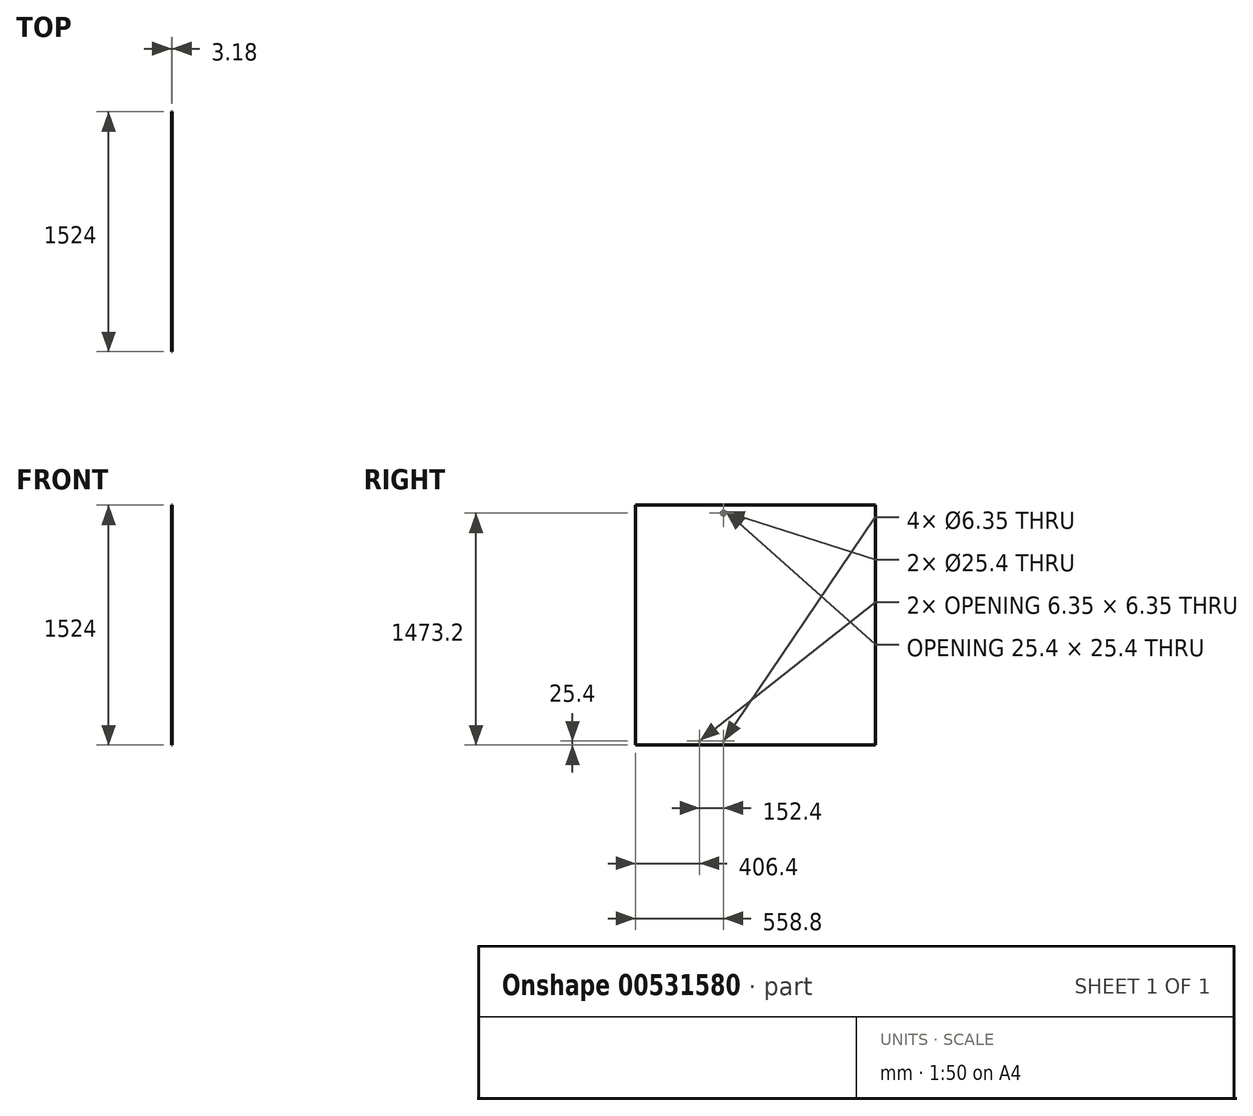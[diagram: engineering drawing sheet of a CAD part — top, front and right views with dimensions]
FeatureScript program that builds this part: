
annotation { "Feature Type Name" : "Feature", "Feature Type Description" : "" }
export const myFeature = defineFeature(function(context is Context, id is Id, definition is map)
    precondition{}
    {
        {
            var Q0;
            Q0=qCreatedBy(makeId("Right.planeOp"),FACE);
            var sketch = newSketch(context, id + "F0", { "sketchPlane" : qUnion([Q0])});
            skLineSegment(sketch, "E0.bottom", {"start": v(0, 0) * mm, "end": v(0, 0) * mm});
            skLineSegment(sketch, "E0.top", {"start": v(0, 0) * mm, "end": v(0, 0) * mm});
            skLineSegment(sketch, "E0.left", {"start": v(0, 0) * mm, "end": v(0, 0) * mm});
            skLineSegment(sketch, "E0.right", {"start": v(0, 0) * mm, "end": v(0, 0) * mm});
            skLineSegment(sketch, "E1.bottom", {"start": v(1524, 1524) * mm, "end": v(0, 1524) * mm});
            skLineSegment(sketch, "E1.top", {"start": v(1524, 0) * mm, "end": v(0, 0) * mm});
            skLineSegment(sketch, "E1.left", {"start": v(1524, 1524) * mm, "end": v(1524, 0) * mm});
            skLineSegment(sketch, "E1.right", {"start": v(0, 1524) * mm, "end": v(0, 0) * mm});
            skPoint(sketch, "E2", {"position": v(406.4, 25.4) * mm});
            skPoint(sketch, "E3", {"position": v(558.8, 25.4) * mm});
            skPoint(sketch, "E4", {"position": v(558.8, 1473.2) * mm});
            skSolve(sketch);
        }
        {
            var Q0;
            Q0=makeQuery(id+"F0.imprint","IMPRINT",FACE,{"disambiguationData":[TD([[makeQuery(id+"F0.imprint","IMPRINT",EDGE,{"derivedFrom":sQuery(id+"F0.wireOp",EDGE,"E1.bottom")}),1.0]])]});
            extrude(context, id + "F1", {"entities" : qUnion([Q0]), "depth" : 3.17 * mm, "offsetDistance" : 25.4 * mm});
        }
        {
            var Q0;
            Q0=sQuery(id+"F0.wireOp",VERTEX,"E2");
            var Q1;
            Q1=makeQuery(id+"F1.opExtrude","SWEPT_BODY",BODY,{"disambiguationData":[OSD([sQuery(id+"F0.wireOp",EDGE,"E1.bottom"),sQuery(id+"F0.wireOp",EDGE,"E1.top"),sQuery(id+"F0.wireOp",EDGE,"E1.left"),sQuery(id+"F0.wireOp",EDGE,"E1.right")])]});
            hole(context, id + "F2", {"style" : HoleStyle.SIMPLE, "endStyle" : HoleEndStyle.THROUGH, "oppositeDirection" : true, "holeDiameter" : 6.35 * mm, "isTappedThrough" : true, "tappedDepth" : 12.7 * mm, "tapClearance" : 3, "locations" : qUnion([Q0]), "scope" : qUnion([Q1])});
        }
        {
            var Q0;
            Q0=sQuery(id+"F0.wireOp",VERTEX,"E3");
            var Q1;
            Q1=makeQuery(id+"F1.opExtrude","SWEPT_BODY",BODY,{"disambiguationData":[OSD([sQuery(id+"F0.wireOp",EDGE,"E1.bottom"),sQuery(id+"F0.wireOp",EDGE,"E1.top"),sQuery(id+"F0.wireOp",EDGE,"E1.left"),sQuery(id+"F0.wireOp",EDGE,"E1.right")])]});
            hole(context, id + "F3", {"style" : HoleStyle.SIMPLE, "endStyle" : HoleEndStyle.THROUGH, "oppositeDirection" : true, "holeDiameter" : 6.35 * mm, "isTappedThrough" : true, "tappedDepth" : 12.7 * mm, "tapClearance" : 3, "locations" : qUnion([Q0]), "scope" : qUnion([Q1])});
        }
        {
            var Q0;
            Q0=sQuery(id+"F0.wireOp",VERTEX,"E4");
            var Q1;
            Q1=makeQuery(id+"F1.opExtrude","SWEPT_BODY",BODY,{"disambiguationData":[OSD([sQuery(id+"F0.wireOp",EDGE,"E1.bottom"),sQuery(id+"F0.wireOp",EDGE,"E1.top"),sQuery(id+"F0.wireOp",EDGE,"E1.left"),sQuery(id+"F0.wireOp",EDGE,"E1.right")])]});
            hole(context, id + "F4", {"style" : HoleStyle.SIMPLE, "endStyle" : HoleEndStyle.THROUGH, "oppositeDirection" : true, "holeDiameter" : 25.4 * mm, "isTappedThrough" : true, "tappedDepth" : 12.7 * mm, "tapClearance" : 3, "locations" : qUnion([Q0]), "scope" : qUnion([Q1])});
        }
    });
